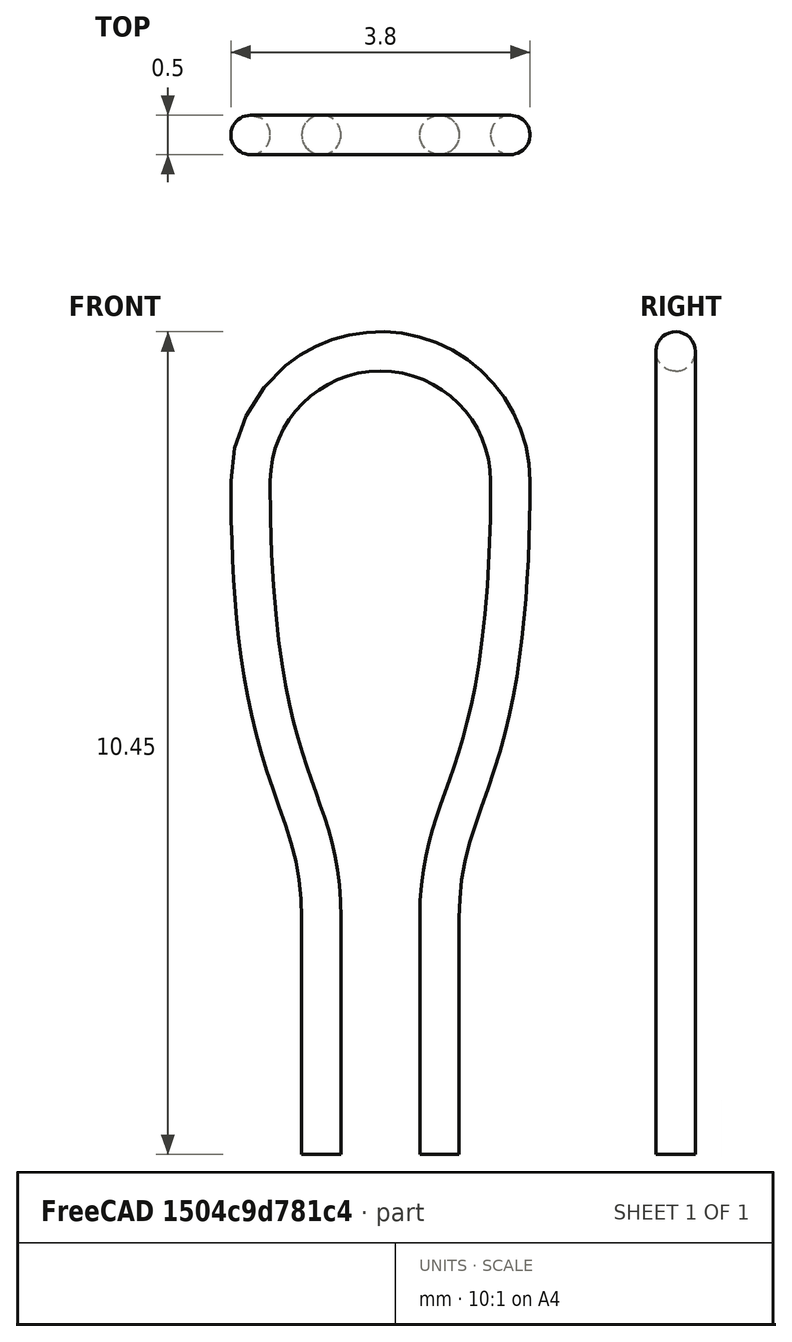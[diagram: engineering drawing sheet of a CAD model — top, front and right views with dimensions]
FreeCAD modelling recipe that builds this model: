
FCSTD DOCUMENT  (FreeCAD 0.17R12018 (Git))
Label: Test_Point_Loop_D3.80mm_Drill2.0mm
License: All rights reserved
LicenseURL: http://en.wikipedia.org/wiki/All_rights_reserved
objects: Sketcher::SketchObject×2, Spreadsheet::Sheet×1, PartDesign::AdditivePipe×1, PartDesign::Body×1, App::Part×1
note: 5 computed .brp shape members not serialized (recipe doc carries the construction recipe); baked Part::Feature solids carry a one-line shape summary decoded from their .brp

FEATURE [Spreadsheet::Sheet] Spreadsheet  label="dims"
  cells = A1="DWire"; B1(DWire)=0.5; A2="DLoop"; B2(DLoop)=3.7999999999999998; A3="Spacer"; B3(Spacer)=0; A4="DSpacer"; B4(DSpacer)=3; A5="Lall"; B5(Lall)=10.199999999999999; A6="Ddrill"; B6(Ddrill)=2; A7="Lbottom"; B7(Lbottom)=3
FEATURE [Sketcher::SketchObject] Sketch001
  MapMode = 5
  Placement = pos=(0,0,0) rot=(1,0,0;1.5708rad)
  expr: Constraints[63] = (dims.DLoop - dims.DWire) / 2
  expr: Constraints[28] = dims.Lall - (dims.DLoop - dims.DWire) / 2
  expr: Constraints[27] = (dims.DLoop - dims.DWire) / 2
  expr: Constraints[30] = dims.Lbottom
  expr: Constraints[32] = dims.Spacer
  expr: Constraints[33] = dims.Ddrill - dims.DWire
  expr: Constraints[34] = (dims.Ddrill - dims.DWire) / 2
  sketch-geometry (25):
    g0: LineSegment StartX=-0.749998 StartY=-3 StartZ=0 EndX=-0.749998 EndY=-1.6e-10 EndZ=0
    g1: LineSegment StartX=0.750004 StartY=-3.34e-10 StartZ=0 EndX=0.750004 EndY=-3 EndZ=0
    g2: ArcOfCircle CenterX=0 CenterY=5.55 CenterZ=0 NormalX=0 NormalY=0 NormalZ=1 Radius=1.65 StartAngle=-1.6e-11 EndAngle=3.14159
    g3: LineSegment [constr] StartX=-1.65 StartY=5.55 StartZ=0 EndX=1.65 EndY=5.55 EndZ=0
    g4: LineSegment [constr] StartX=-1.65 StartY=-3.09e-10 StartZ=0 EndX=1.65 EndY=-3.09e-10 EndZ=0
    g5: LineSegment [constr] StartX=1.65 StartY=5.55 StartZ=0 EndX=1.65 EndY=-3.09e-10 EndZ=0
    g6: LineSegment [constr] StartX=-1.65 StartY=-3.09e-10 StartZ=0 EndX=-1.65 EndY=5.55 EndZ=0
    g7: LineSegment [constr] StartX=-0.749998 StartY=-1.6e-10 StartZ=0 EndX=-0.749998 EndY=1.65 EndZ=0
    g8: LineSegment [constr] StartX=0.750004 StartY=-3.34e-10 StartZ=0 EndX=0.750004 EndY=1.65 EndZ=0
    g9: LineSegment [constr] StartX=-1.65 StartY=1.65 StartZ=0 EndX=1.65 EndY=1.65 EndZ=0
    g10: LineSegment [constr] StartX=0.750004 StartY=1.65 StartZ=0 EndX=0.750004 EndY=5.55 EndZ=0
    g11-g14: Circle [constr] x4 (B-spline internal-alignment scaffolding for g15; pole/knot coordinates omitted)
    g15: BSplineCurve PolesCount=4 KnotsCount=2 Degree=3 IsPeriodic=0
    g16: GeomPoint [constr] X=-0.749998 Y=-1.6e-10 Z=0
    g17: GeomPoint [constr] X=-1.65 Y=5.55 Z=0
    g18-g21: Circle [constr] x4 (B-spline internal-alignment scaffolding for g22; pole/knot coordinates omitted)
    g22: BSplineCurve PolesCount=4 KnotsCount=2 Degree=3 IsPeriodic=0
    g23: GeomPoint [constr] X=0.750004 Y=-3.34e-10 Z=0
    g24: GeomPoint [constr] X=1.65 Y=5.55 Z=0
  constraints (58):
    c: Vertical(g0)
    c: Vertical(g1)
    c: Coincident(g3,g2)
    c: Horizontal(g3)
    c: PointOnObject(g2,g3)
    c: Coincident(g3,g2)
    c: PointOnObject(g2,g-2)
    c: Horizontal(g4)
    c: Coincident(g5,g2)
    c: Coincident(g5,g4)
    c: Coincident(g6,g4)
    c: Coincident(g6,g2)
    c: PointOnObject(g0,g4)
    c: PointOnObject(g1,g4)
    c: Vertical(g6)
    c: Vertical(g5)
    c: Coincident(g7,g0)
    c: Vertical(g7)
    c: Coincident(g8,g1)
    c: Vertical(g8)
    c: PointOnObject(g9,g6)
    c: PointOnObject(g9,g5)
    c: Horizontal(g9)
    c: PointOnObject(g7,g9)
    c: PointOnObject(g8,g9)
    c: PointOnObject(g10,g3)
    c: Vertical(g10)
    c: Radius(g2) = 1.65
    c: DistanceY(g1,g2) = 8.55
    c: DistanceY(g1,g0) = 0
    c: DistanceY(g0,g-1) = 3
    c: Coincident(g10,g8)
    c: DistanceY(g-1,g0) = 0
    c: DistanceX(g0,g1) = 1.5
    c: DistanceX(g0,g-1) = 0.75
    c: Coincident(g11,g0)
    c: Radius(g11) = 0
    c: Equal(g11,g12)
    c: Coincident(g12,g7)
    c: Equal(g11,g13)
    c: Coincident(g13,g9)
    c: Equal(g11,g14)
    c: Coincident(g14,g2)
    c: InternalAlignment(g11-g14 -> g15) x4
    c: InternalAlignment(g16,g15)
    c: InternalAlignment(g17,g15)
    c: Coincident(g18,g1)
    c: Radius(g18) = 0
    c: Equal(g18,g19)
    c: Coincident(g19,g8)
    c: Equal(g18,g20)
    c: Coincident(g20,g9)
    c: Equal(g18,g21)
    c: Coincident(g21,g2)
    c: InternalAlignment(g18-g21 -> g22) x4
    c: InternalAlignment(g23,g22)
    c: InternalAlignment(g24,g22)
    c: DistanceY(g4,g9) = 1.65
FEATURE [Sketcher::SketchObject] Sketch
  MapMode = 5
  Placement = pos=(0,0,-3) rot=(0,0,1;0rad)
  expr: Constraints[2] = (dims.Ddrill - dims.DWire) / 2
  expr: Constraints[1] = dims.DWire / 2
  sketch-geometry (1):
    g0: Circle CenterX=-0.75 CenterY=0 CenterZ=0 NormalX=0 NormalY=0 NormalZ=1 Radius=0.25
  constraints (3):
    c: PointOnObject(g0,g-1)
    c: Radius(g0) = 0.25
    c: DistanceX(g0,g-1) = 0.75
FEATURE [PartDesign::AdditivePipe] AdditivePipe
  AuxilleryCurvelinear = true
  AuxillerySpineTangent = false
  Binormal = (0,0,0)
  Mode = 0
  Placement = pos=(0,0,-3) rot=(0,0,1;0rad)
  Profile = -> Sketch
  Spine = -> Sketch001 [Edge1,Edge2,Edge3,Edge4,Edge5]
  SpineTangent = false
  Transformation = 0
  Transition = 0
FEATURE [PartDesign::Body] Body  label="Test_Point_Loop_D3.80mm_Drill2.0mm"
  Group = -> [Sketch,Sketch001,AdditivePipe]
  Origin = -> Origin002
  Tip = -> AdditivePipe
FEATURE [App::Part] Part  label="group"
  Group = -> [Body]
  License = CC BY 3.0
  LicenseURL = http://creativecommons.org/licenses/by/3.0/
  Origin = -> Origin
